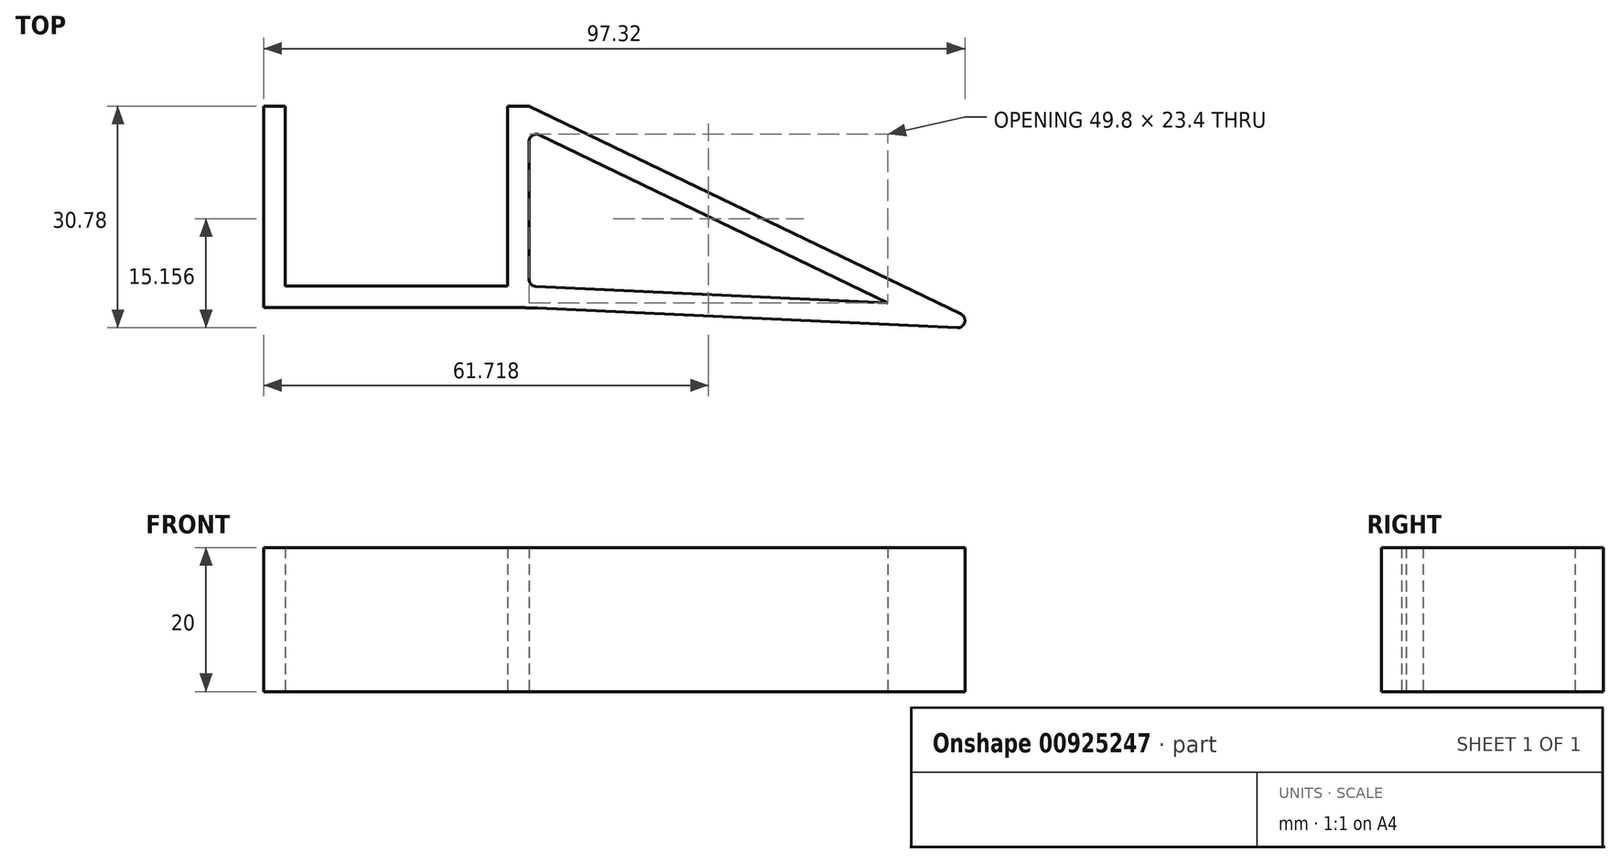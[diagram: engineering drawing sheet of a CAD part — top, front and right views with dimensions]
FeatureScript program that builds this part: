
annotation { "Feature Type Name" : "Feature", "Feature Type Description" : "" }
export const myFeature = defineFeature(function(context is Context, id is Id, definition is map)
    precondition{}
    {
        {
            assignVariable(context, id + "F0", {"name" : "ClipWidth", "anyValue" : 20});
        }
        {
            var Q0;
            Q0=qCreatedBy(makeId("Top.planeOp"),FACE);
            var sketch = newSketch(context, id + "F1", { "sketchPlane" : qUnion([Q0])});
            skLineSegment(sketch, "E0.bottom", {"start": v(-1.17, 0) * mm, "end": v(-36.82, 0) * mm});
            skLineSegment(sketch, "E0.top", {"start": v(0, 28) * mm, "end": v(-3, 28) * mm});
            skLineSegment(sketch, "E0.left", {"start": v(0, 3.96) * mm, "end": v(0, 23.08) * mm});
            skLineSegment(sketch, "E0.right", {"start": v(-36.82, 0) * mm, "end": v(-36.82, 28) * mm});
            skLineSegment(sketch, "E1.top", {"start": v(-33.82, 3) * mm, "end": v(-3, 3) * mm});
            skLineSegment(sketch, "E1.left", {"start": v(-33.82, 28) * mm, "end": v(-33.82, 3) * mm});
            skLineSegment(sketch, "E1.right", {"start": v(-3, 28) * mm, "end": v(-3, 3) * mm});
            skLineSegment(sketch, "E2.trimOffspring", {"start": v(-33.82, 28) * mm, "end": v(-36.82, 28) * mm});
            skLineSegment(sketch, "E3", {"start": v(1.17, -0.05) * mm, "end": v(59.45, -2.78) * mm});
            skLineSegment(sketch, "E4", {"start": v(59.93, -0.88) * mm, "end": v(0, 28) * mm});
            skLineSegment(sketch, "E5", {"start": v(0.95, 2.96) * mm, "end": v(49.8, 0.68) * mm});
            skLineSegment(sketch, "E6", {"start": v(49.8, 0.68) * mm, "end": v(1.43, 23.98) * mm});
            skPoint(sketch, "E7.visualSharp", {"position": v(64.35, -3) * mm});
            skArc(sketch, "E7.filletArc", {"start": v(59.45, -2.78) * mm, "mid": v(60.47, -2.03) * mm, "end": v(59.93, -0.88) * mm});
            skPoint(sketch, "E8.visualSharp", {"position": v(0, 0) * mm});
            skArc(sketch, "E8.filletArc", {"start": v(1.17, -0.05) * mm, "mid": v(0, -0.01) * mm, "end": v(-1.17, 0) * mm});
            skPoint(sketch, "E9.visualSharp", {"position": v(0, 24.67) * mm});
            skArc(sketch, "E9.filletArc", {"start": v(1.43, 23.98) * mm, "mid": v(0.47, 23.92) * mm, "end": v(0, 23.08) * mm});
            skPoint(sketch, "E10.visualSharp", {"position": v(0, 3) * mm});
            skArc(sketch, "E10.filletArc", {"start": v(0, 3.96) * mm, "mid": v(0.28, 3.27) * mm, "end": v(0.95, 2.96) * mm});
            skSolve(sketch);
        }
        {
            var Q0;
            Q0=makeQuery(id+"F1.imprint","IMPRINT",FACE,{"disambiguationData":[TD([[makeQuery(id+"F1.imprint","IMPRINT",EDGE,{"derivedFrom":sQuery(id+"F1.wireOp",EDGE,"E0.bottom")}),-1.0]])]});
            extrude(context, id + "F2", {"entities" : qUnion([Q0]), "depth" : (getVariable(context, 'ClipWidth')) * mm, "offsetDistance" : 25 * mm});
        }
    });
